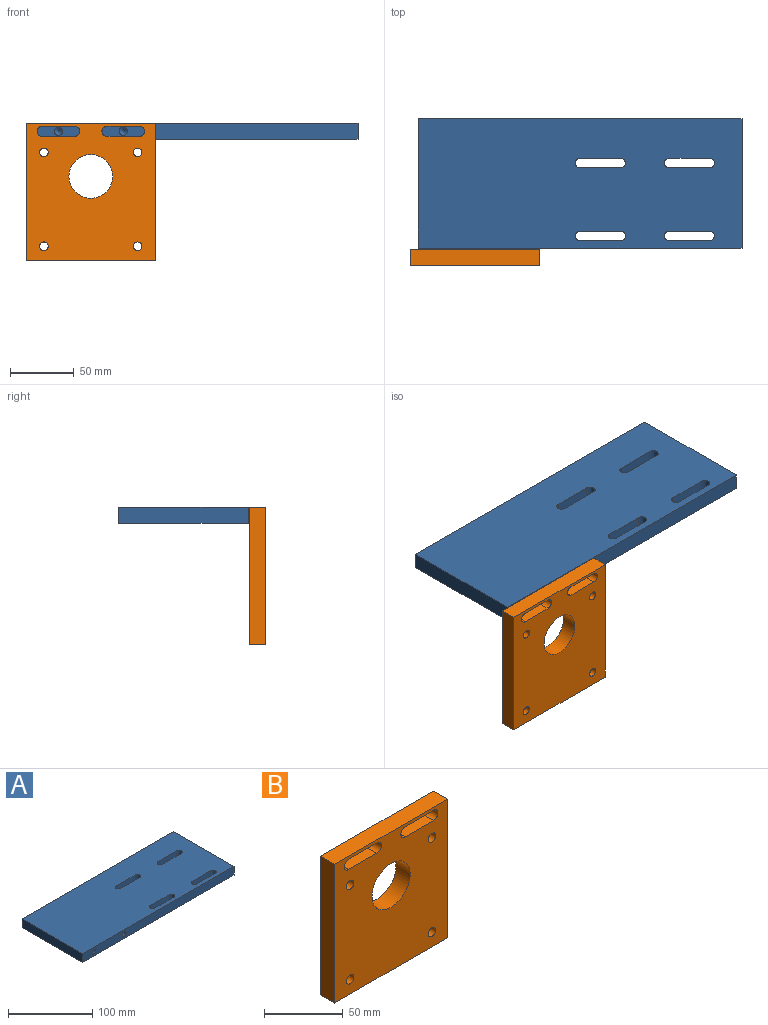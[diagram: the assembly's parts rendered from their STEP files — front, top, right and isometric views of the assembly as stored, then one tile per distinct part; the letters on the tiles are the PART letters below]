
ASSEMBLY  parts=2 mates=1
PART A: 26 faces, bbox 254x101.6x12.7 mm
  f0: plane 254x101.6mm, normal (0,0,1), area 24674.3mm2, adj f2,f3,f4,f5,f10,f11,f12,f13
  f1: plane 254x101.6mm, normal (0,0,-1), area 24674.3mm2, adj f2,f3,f4,f5,f10,f11,f12,f13
  f2: plane 101.6x12.7mm, normal (1,0,0), area 1290.3mm2, adj f0,f1,f4,f5
  f3: plane 101.6x12.7mm, normal (-1,0,0), area 1290.3mm2, adj f0,f1,f4,f5
  f4: plane 254x12.7mm, normal (0,-1,0), area 3158.9mm2, adj f0,f1,f2,f3,f7,f9
  f5: plane 254x12.7mm, normal (0,1,0), area 3225.8mm2, adj f0,f1,f2,f3
  f6: cone r=0mm half-angle=59deg, axis (0,-1,0), area 39mm2, adj f7
  f7: cylinder r=3.26mm len=29.63mm, axis (0,-1,0), area 607.7mm2, adj f4,f6
  f8: cone r=0mm half-angle=59deg, axis (0,-1,0), area 39mm2, adj f9
  f9: cylinder r=3.26mm len=29.63mm, axis (0,-1,0), area 607.7mm2, adj f4,f8
  f10: plane 31.67x12.7mm, normal (0,1,0), area 402.2mm2, adj f0,f1,f11,f13
  f11: cylinder r=3.76mm len=12.7mm, axis (0,0,1), area 149.2mm2, adj f0,f1,f10,f12
  f12: plane 31.75x12.7mm, normal (0,-1,0), area 403.2mm2, adj f0,f1,f11,f13
  f13: cylinder r=3.76mm len=12.7mm, axis (0,0,1), area 151.8mm2, adj f0,f1,f10,f12
  f14: plane 31.67x12.7mm, normal (0,1,0), area 402.2mm2, adj f0,f1,f15,f17
  f15: cylinder r=3.76mm len=12.7mm, axis (0,0,1), area 149.2mm2, adj f0,f1,f14,f16
  f16: plane 31.75x12.7mm, normal (0,-1,0), area 403.2mm2, adj f0,f1,f15,f17
  f17: cylinder r=3.76mm len=12.7mm, axis (0,0,1), area 151.8mm2, adj f0,f1,f14,f16
  f18: plane 31.75x12.7mm, normal (0,-1,0), area 403.2mm2, adj f0,f1,f19,f21
  f19: cylinder r=3.76mm len=12.7mm, axis (0,0,1), area 150mm2, adj f0,f1,f18,f20
  f20: plane 31.69x12.7mm, normal (0,1,0), area 402.5mm2, adj f0,f1,f19,f21
  f21: cylinder r=3.76mm len=12.7mm, axis (0,0,1), area 150.7mm2, adj f0,f1,f18,f20
  f22: plane 32.03x12.7mm, normal (0,-1,0), area 406.8mm2, adj f0,f1,f23,f25
  f23: cylinder r=3.76mm len=12.7mm, axis (0,0,1), area 146.4mm2, adj f0,f1,f22,f24
  f24: plane 31.73x12.7mm, normal (0,1,0), area 402.9mm2, adj f0,f1,f23,f25
  f25: cylinder r=3.76mm len=12.7mm, axis (0,0,1), area 150.3mm2, adj f0,f1,f22,f24
PART B: 19 faces, bbox 101.6x12.7x108 mm
  f0: plane 107.95x101.6mm, normal (0,-1,0), area 9398.6mm2, adj f2,f3,f4,f5,f6,f7,f8,f9
  f1: plane 107.95x101.6mm, normal (0,1,0), area 9398.6mm2, adj f2,f3,f4,f5,f6,f7,f8,f9
  f2: plane 107.95x12.7mm, normal (1,0,0), area 1371mm2, adj f0,f1,f3,f5
  f3: plane 101.6x12.7mm, normal (0,0,1), area 1290.3mm2, adj f0,f1,f2,f4
  f4: plane 107.95x12.7mm, normal (-1,0,0), area 1371mm2, adj f0,f1,f3,f5
  f5: plane 101.6x12.7mm, normal (0,0,-1), area 1290.3mm2, adj f0,f1,f2,f4
  f6: cylinder r=3.38mm len=12.7mm, axis (0,-1,0), area 269.6mm2, adj f0,f1
  f7: cylinder r=3.38mm len=12.7mm, axis (0,-1,0), area 269.6mm2, adj f0,f1
  f8: cylinder r=3.38mm len=12.7mm, axis (0,-1,0), area 269.6mm2, adj f0,f1
  f9: cylinder r=3.38mm len=12.7mm, axis (0,-1,0), area 269.6mm2, adj f0,f1
  f10: cylinder r=17.14mm len=34.29mm, axis (0,-1,0), area 1368.1mm2, adj f0,f1
  f11: plane 25.4x12.7mm, normal (0,0,-1), area 322.6mm2, adj f0,f1,f12,f14
  f12: cylinder r=3.97mm len=12.7mm, axis (0,-1,0), area 158.3mm2, adj f0,f1,f11,f13
  f13: plane 25.4x12.7mm, normal (0,0,1), area 322.6mm2, adj f0,f1,f12,f14
  f14: cylinder r=3.97mm len=12.7mm, axis (0,-1,0), area 158.3mm2, adj f0,f1,f11,f13
  f15: plane 25.4x12.7mm, normal (0,0,1), area 322.6mm2, adj f0,f1,f16,f18
  f16: cylinder r=3.97mm len=12.7mm, axis (0,-1,0), area 158.3mm2, adj f0,f1,f15,f17
  f17: plane 25.4x12.7mm, normal (0,0,-1), area 322.6mm2, adj f0,f1,f16,f18
  f18: cylinder r=3.97mm len=12.7mm, axis (0,-1,0), area 158.3mm2, adj f0,f1,f15,f17
PLACE A t=(50.76,41.8,90.29)mm
PLACE B t=(-31.79,-60.55,42.67)mm
MATE pin_slot B.f0 <-> A.f8  axis (0,-1,0) through (-57.19,-73.25,90.29)mm
